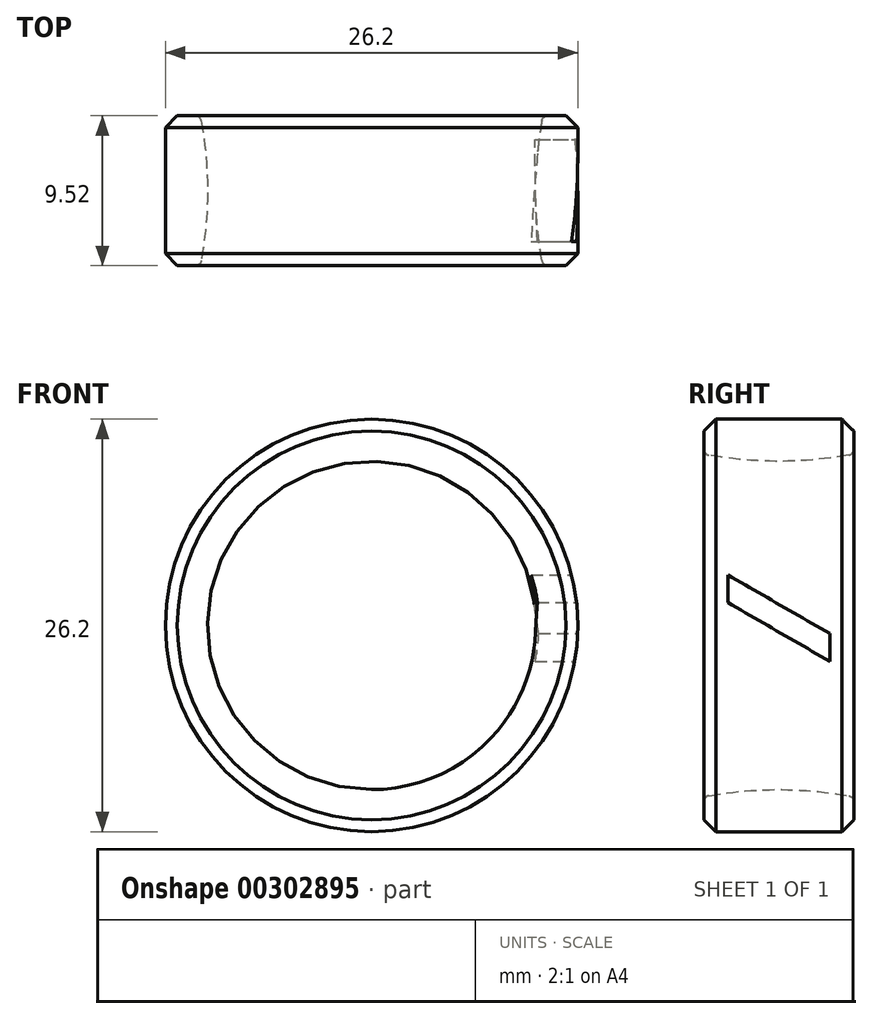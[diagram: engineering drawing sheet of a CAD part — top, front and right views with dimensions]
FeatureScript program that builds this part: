
annotation { "Feature Type Name" : "Feature", "Feature Type Description" : "" }
export const myFeature = defineFeature(function(context is Context, id is Id, definition is map)
    precondition{}
    {
        {
            var Q0;
            Q0=qCreatedBy(makeId("Top.planeOp"),FACE);
            var sketch = newSketch(context, id + "F0", { "sketchPlane" : qUnion([Q0])});
            skLineSegment(sketch, "E0", {"start": v(0, 0) * mm, "end": v(-22.97, 0) * mm});
            skArc(sketch, "E1", {"start": v(-10.88, -4.76) * mm, "mid": v(-10.43, 0) * mm, "end": v(-10.88, 4.76) * mm});
            skLineSegment(sketch, "E2.bottom", {"start": v(-13.1, 4.76) * mm, "end": v(-10.88, 4.76) * mm});
            skLineSegment(sketch, "E2.top", {"start": v(-13.1, -4.76) * mm, "end": v(-10.88, -4.76) * mm});
            skLineSegment(sketch, "E2.left", {"start": v(-13.1, 4.76) * mm, "end": v(-13.1, -4.76) * mm});
            skLineSegment(sketch, "E3", {"start": v(0, 0) * mm, "end": v(0, 12.06) * mm});
            skSolve(sketch);
        }
        {
            var Q0;
            {var subQ5=sQuery(id+"F0.wireOp",EDGE,"E2.bottom");Q0=makeQuery(id+"F0.imprint","IMPRINT",FACE,{"disambiguationData":[TD([[makeQuery(id+"F0.imprint","IMPRINT",EDGE,{"derivedFrom":subQ5}),-1.0]])]});}
            var Q1;
            {var subQ5=sQuery(id+"F0.wireOp",EDGE,"E2.top");Q1=makeQuery(id+"F0.imprint","IMPRINT",FACE,{"disambiguationData":[TD([[makeQuery(id+"F0.imprint","IMPRINT",EDGE,{"derivedFrom":subQ5}),1.0]])]});}
            var Q2;
            Q2=sQuery(id+"F0.wireOp",EDGE,"E3");
            revolve(context, id + "F1", {"entities" : qUnion([Q0, Q1]), "axis" : qUnion([Q2]), "revolveType" : RevolveType.FULL});
        }
        {
            var Q0;
            Q0=makeQuery(id+"F1.opRevolve","SWEPT_EDGE",EDGE,{"disambiguationData":[OSD([sQuery(id+"F0.wireOp",EDGE,"E2.bottom"),sQuery(id+"F0.wireOp",EDGE,"E2.left")])]});
            var Q1;
            Q1=makeQuery(id+"F1.opRevolve","SWEPT_EDGE",EDGE,{"disambiguationData":[OSD([sQuery(id+"F0.wireOp",EDGE,"E2.top"),sQuery(id+"F0.wireOp",EDGE,"E2.left")])]});
            chamfer(context, id + "F2", {"entities" : qUnion([Q0, Q1]), "width" : 0.76 * mm, "tangentPropagation" : true});
        }
        {
            var Q0;
            Q0=makeQuery(id+"F1.opRevolve","SWEPT_EDGE",EDGE,{"disambiguationData":[OSD([sQuery(id+"F0.wireOp",EDGE,"E1"),sQuery(id+"F0.wireOp",EDGE,"E2.top")])]});
            var Q1;
            Q1=makeQuery(id+"F1.opRevolve","SWEPT_EDGE",EDGE,{"disambiguationData":[OSD([sQuery(id+"F0.wireOp",EDGE,"E1"),sQuery(id+"F0.wireOp",EDGE,"E2.bottom")])]});
            fillet(context, id + "F3", {"entities" : qUnion([Q0, Q1]), "radius" : 0.38 * mm, "tangentPropagation" : true, "allowEdgeOverflow" : false});
        }
        {
            var Q0;
            Q0=qCreatedBy(makeId("Right.planeOp"),FACE);
            cPlane(context, id + "F4", {"entities" : qUnion([Q0]), "cplaneType" : CPlaneType.OFFSET, "offset" : 15.5 * mm, "width" : 152.4 * mm, "height" : 152.4 * mm});
        }
        {
            var Q0;
            Q0=qCreatedBy(id+"F4.planeOp",FACE);
            var sketch = newSketch(context, id + "F5", { "sketchPlane" : qUnion([Q0])});
            skLineSegment(sketch, "E4", {"start": v(3.24, -0.52) * mm, "end": v(-3.24, 3.22) * mm});
            skLineSegment(sketch, "E5", {"start": v(-3.24, 3.22) * mm, "end": v(-3.24, 1.46) * mm});
            skLineSegment(sketch, "E6", {"start": v(-3.24, 1.46) * mm, "end": v(3.24, -2.28) * mm});
            skLineSegment(sketch, "E7", {"start": v(3.24, -2.28) * mm, "end": v(3.24, -0.52) * mm});
            skSolve(sketch);
        }
        {
            var Q0;
            Q0=makeQuery(id+"F5.imprint","IMPRINT",FACE,{"disambiguationData":[TD([[makeQuery(id+"F5.imprint","IMPRINT",EDGE,{"derivedFrom":sQuery(id+"F5.wireOp",EDGE,"E4")}),1.0]])]});
            extrude(context, id + "F6", {"entities" : qUnion([Q0]), "operationType" : NewBodyOperationType.REMOVE, "oppositeDirection" : true, "depth" : 6.35 * mm});
        }
    });
